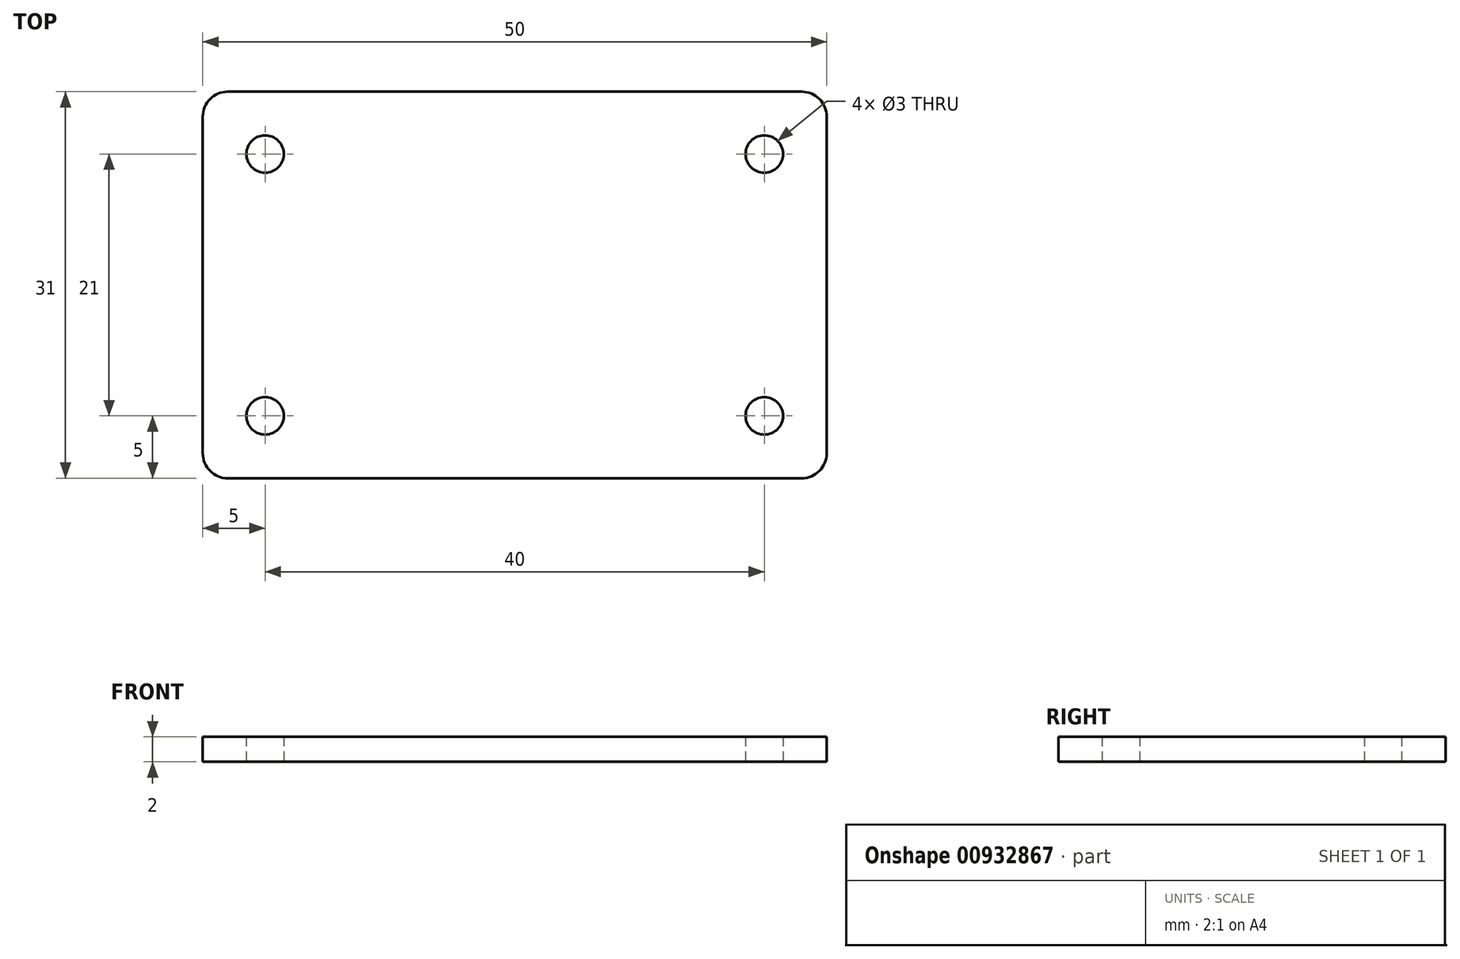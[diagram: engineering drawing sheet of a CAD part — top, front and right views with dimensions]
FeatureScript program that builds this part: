
annotation { "Feature Type Name" : "Feature", "Feature Type Description" : "" }
export const myFeature = defineFeature(function(context is Context, id is Id, definition is map)
    precondition{}
    {
        {
            var Q0;
            Q0=qCreatedBy(makeId("Top.planeOp"),FACE);
            var sketch = newSketch(context, id + "F0", { "sketchPlane" : qUnion([Q0])});
            skLineSegment(sketch, "E0.bottom", {"start": v(0, 0) * mm, "end": v(50, 0) * mm});
            skLineSegment(sketch, "E0.top", {"start": v(0, 31) * mm, "end": v(50, 31) * mm});
            skLineSegment(sketch, "E0.left", {"start": v(0, 0) * mm, "end": v(0, 31) * mm});
            skLineSegment(sketch, "E0.right", {"start": v(50, 0) * mm, "end": v(50, 31) * mm});
            skCircle(sketch, "E1", {"center": v(5, 26) * mm, "radius": 1.5 * mm});
            skLineSegment(sketch, "E2", {"start": v(0, 15.5) * mm, "end": v(50, 15.5) * mm, "construction": true});
            skLineSegment(sketch, "E3", {"start": v(25, 31) * mm, "end": v(25, 0) * mm, "construction": true});
            skCircle(sketch, "E4.MirrorC", {"center": v(5, 5) * mm, "radius": 1.5 * mm});
            skCircle(sketch, "E5.MirrorC", {"center": v(45, 26) * mm, "radius": 1.5 * mm});
            skCircle(sketch, "E6.MirrorC", {"center": v(45, 5) * mm, "radius": 1.5 * mm});
            skSolve(sketch);
        }
        {
            var Q0;
            Q0=makeQuery(id+"F0.imprint","IMPRINT",FACE,{"disambiguationData":[TD([[makeQuery(id+"F0.imprint","IMPRINT",EDGE,{"derivedFrom":sQuery(id+"F0.wireOp",EDGE,"E0.bottom")}),1.0]])]});
            extrude(context, id + "F1", {"entities" : qUnion([Q0]), "depth" : 2 * mm, "offsetDistance" : 25 * mm});
        }
        {
            var Q0;
            Q0=makeQuery(id+"F1.opExtrude","SWEPT_EDGE",EDGE,{"disambiguationData":[OSD([sQuery(id+"F0.wireOp",EDGE,"E0.bottom"),sQuery(id+"F0.wireOp",EDGE,"E0.left")])]});
            var Q1;
            Q1=makeQuery(id+"F1.opExtrude","SWEPT_EDGE",EDGE,{"disambiguationData":[OSD([sQuery(id+"F0.wireOp",EDGE,"E0.top"),sQuery(id+"F0.wireOp",EDGE,"E0.left")])]});
            var Q2;
            Q2=makeQuery(id+"F1.opExtrude","SWEPT_EDGE",EDGE,{"disambiguationData":[OSD([sQuery(id+"F0.wireOp",EDGE,"E0.bottom"),sQuery(id+"F0.wireOp",EDGE,"E0.right")])]});
            var Q3;
            Q3=makeQuery(id+"F1.opExtrude","SWEPT_EDGE",EDGE,{"disambiguationData":[OSD([sQuery(id+"F0.wireOp",EDGE,"E0.top"),sQuery(id+"F0.wireOp",EDGE,"E0.right")])]});
            fillet(context, id + "F2", {"entities" : qUnion([Q0, Q1, Q2, Q3]), "radius" : 2 * mm, "tangentPropagation" : true, "allowEdgeOverflow" : false});
        }
    });
